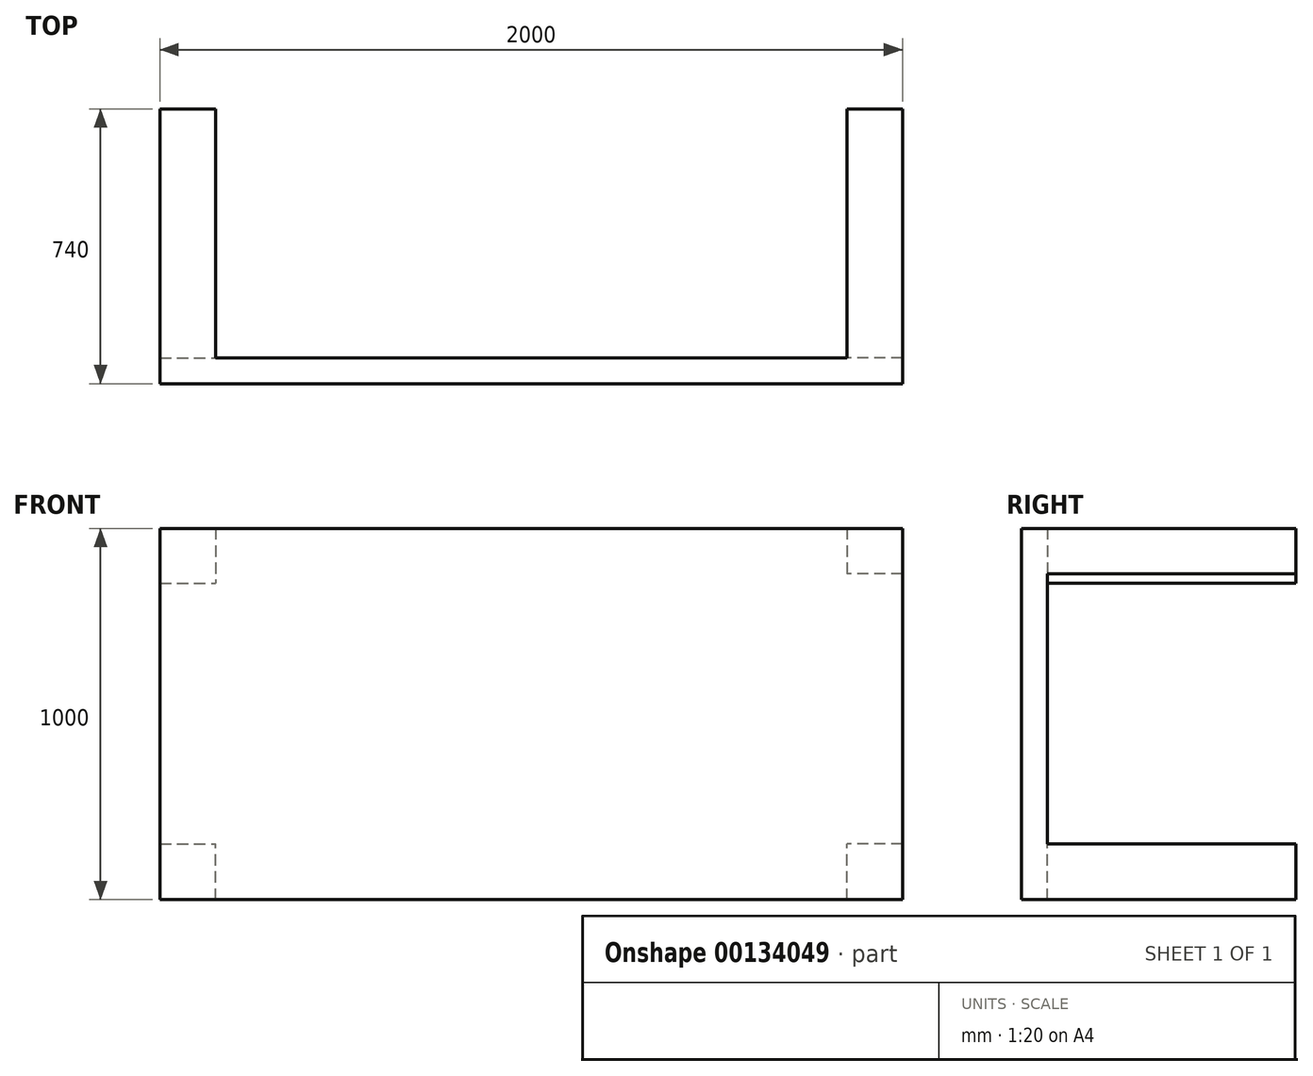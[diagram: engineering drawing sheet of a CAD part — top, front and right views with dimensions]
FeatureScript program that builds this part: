
annotation { "Feature Type Name" : "Feature", "Feature Type Description" : "" }
export const myFeature = defineFeature(function(context is Context, id is Id, definition is map)
    precondition{}
    {
        {
            var Q0;
            Q0=qCreatedBy(makeId("Front.planeOp"),FACE);
            var sketch = newSketch(context, id + "F0", { "sketchPlane" : qUnion([Q0])});
            skLineSegment(sketch, "E0.bottom", {"start": v(-1000.82, -74.1) * mm, "end": v(999.18, -74.1) * mm});
            skLineSegment(sketch, "E0.top", {"start": v(-1000.82, -1074.1) * mm, "end": v(999.18, -1074.1) * mm});
            skLineSegment(sketch, "E0.left", {"start": v(-1000.82, -74.1) * mm, "end": v(-1000.82, -1074.1) * mm});
            skLineSegment(sketch, "E0.right", {"start": v(999.18, -74.1) * mm, "end": v(999.18, -1074.1) * mm});
            skSolve(sketch);
        }
        {
            var Q0;
            Q0=makeQuery(id+"F0.imprint","IMPRINT",FACE,{"disambiguationData":[TD([[makeQuery(id+"F0.imprint","IMPRINT",EDGE,{"derivedFrom":sQuery(id+"F0.wireOp",EDGE,"E0.bottom")}),-1.0]])]});
            extrude(context, id + "F1", {"entities" : qUnion([Q0]), "depth" : 70 * mm});
        }
        {
            var Q0;
            Q0=makeQuery(id+"F1.opExtrude","CAP_FACE",FACE,{"disambiguationData":[OSD([sQuery(id+"F0.wireOp",EDGE,"E0.bottom"),sQuery(id+"F0.wireOp",EDGE,"E0.top"),sQuery(id+"F0.wireOp",EDGE,"E0.left"),sQuery(id+"F0.wireOp",EDGE,"E0.right")])],"isStart":true});
            var sketch = newSketch(context, id + "F2", { "sketchPlane" : qUnion([Q0])});
            skLineSegment(sketch, "E1.bottom", {"start": v(1000.82, -74.1) * mm, "end": v(850.82, -74.1) * mm});
            skLineSegment(sketch, "E1.top", {"start": v(1000.82, -221.35) * mm, "end": v(850.82, -221.35) * mm});
            skLineSegment(sketch, "E1.left", {"start": v(1000.82, -74.1) * mm, "end": v(1000.82, -221.35) * mm});
            skLineSegment(sketch, "E1.right", {"start": v(850.82, -74.1) * mm, "end": v(850.82, -221.35) * mm});
            skLineSegment(sketch, "E2.bottom", {"start": v(1000.82, -1074.1) * mm, "end": v(850.82, -1074.1) * mm});
            skLineSegment(sketch, "E2.top", {"start": v(1000.82, -924.1) * mm, "end": v(850.82, -924.1) * mm});
            skLineSegment(sketch, "E2.left", {"start": v(1000.82, -1074.1) * mm, "end": v(1000.82, -924.1) * mm});
            skLineSegment(sketch, "E2.right", {"start": v(850.82, -1074.1) * mm, "end": v(850.82, -924.1) * mm});
            skLineSegment(sketch, "E3.bottom", {"start": v(-999.18, -1074.1) * mm, "end": v(-849.18, -1074.1) * mm});
            skLineSegment(sketch, "E3.top", {"start": v(-999.18, -924.1) * mm, "end": v(-849.18, -924.1) * mm});
            skLineSegment(sketch, "E3.left", {"start": v(-999.18, -1074.1) * mm, "end": v(-999.18, -924.1) * mm});
            skLineSegment(sketch, "E3.right", {"start": v(-849.18, -1074.1) * mm, "end": v(-849.18, -924.1) * mm});
            skLineSegment(sketch, "E4.bottom", {"start": v(-999.18, -74.1) * mm, "end": v(-849.18, -74.1) * mm});
            skLineSegment(sketch, "E4.top", {"start": v(-999.18, -196.35) * mm, "end": v(-849.18, -196.35) * mm});
            skLineSegment(sketch, "E4.left", {"start": v(-999.18, -74.1) * mm, "end": v(-999.18, -196.35) * mm});
            skLineSegment(sketch, "E4.right", {"start": v(-849.18, -74.1) * mm, "end": v(-849.18, -196.35) * mm});
            skSolve(sketch);
        }
        {
            var Q0;
            Q0=makeQuery(id+"F2.imprint","IMPRINT",FACE,{"disambiguationData":[TD([[makeQuery(id+"F2.imprint","IMPRINT",EDGE,{"derivedFrom":sQuery(id+"F2.wireOp",EDGE,"E4.bottom")}),1.0]])]});
            var Q1;
            Q1=makeQuery(id+"F2.imprint","IMPRINT",FACE,{"disambiguationData":[TD([[makeQuery(id+"F2.imprint","IMPRINT",EDGE,{"derivedFrom":sQuery(id+"F2.wireOp",EDGE,"E3.bottom")}),-1.0]])]});
            var Q2;
            Q2=makeQuery(id+"F2.imprint","IMPRINT",FACE,{"disambiguationData":[TD([[makeQuery(id+"F2.imprint","IMPRINT",EDGE,{"derivedFrom":sQuery(id+"F2.wireOp",EDGE,"E2.bottom")}),-1.0]])]});
            var Q3;
            Q3=makeQuery(id+"F2.imprint","IMPRINT",FACE,{"disambiguationData":[TD([[makeQuery(id+"F2.imprint","IMPRINT",EDGE,{"derivedFrom":sQuery(id+"F2.wireOp",EDGE,"E1.bottom")}),1.0]])]});
            extrude(context, id + "F3", {"entities" : qUnion([Q0, Q1, Q2, Q3]), "operationType" : NewBodyOperationType.ADD, "depth" : 670 * mm});
        }
    });
